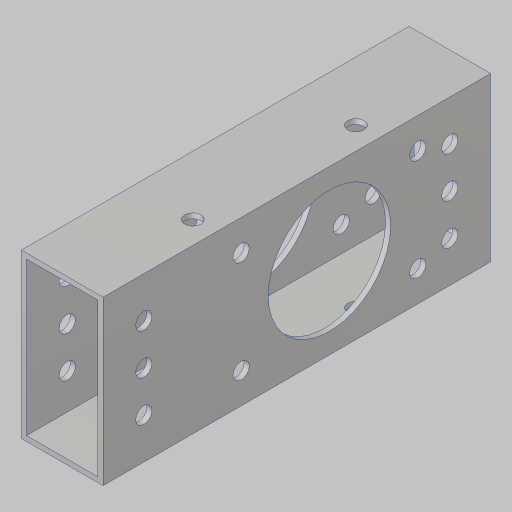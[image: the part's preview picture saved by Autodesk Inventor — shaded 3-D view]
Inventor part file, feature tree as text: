
AUTODESK INVENTOR PART (.ipt)
format: ipt  version: 2023.5 (Build 275446000, 446)  size: 186,368 bytes
history: native  units: in
note: dims shown in document units (in); Inventor stores cm internally (conversion verified against a paired STEP export)
features: extrude x2, sketch x2, hole x2
ambient origin geometry x8: Origin, YZ Plane, XZ Plane, XY Plane, X Axis, Y Axis, Z Axis, Center Point
bodies: Solid1 (feature_tree)
feature tree (6):
  extrude  "Extrusion1"  Depth=2.5in
  sketch  "Sketch2"  dims[d4=0.0in d5=2.5in]
  hole  "Hole1"  [1 undecoded]
  extrude  "Extrusion3"  Depth=2.0in
  hole  "Hole2"  [1 undecoded]
  sketch  "Sketch4"  dims[d10=0.201in d11=0.75in d12=0.385in d13=0.25in d14=0.5635in d15=1.0in d16=0.8108in d17=0.5in d18=0.5in d19=0.5in d23=0.4in d24=2.3622in d26=360.0deg d28=1.5in d29=0.0in d30=0.0in d32=0.201in d33=0.75in d34=0.385in d35=0.25in d36=0.5635in d37=1.0in d38=0.8108in d41=2.0in d42=0.725in]
note: 2 required parameter values undecoded (feature->parameter linkage not recoverable at this tier; creation-order binding heuristic only, values carry confidence <= 0.55)
